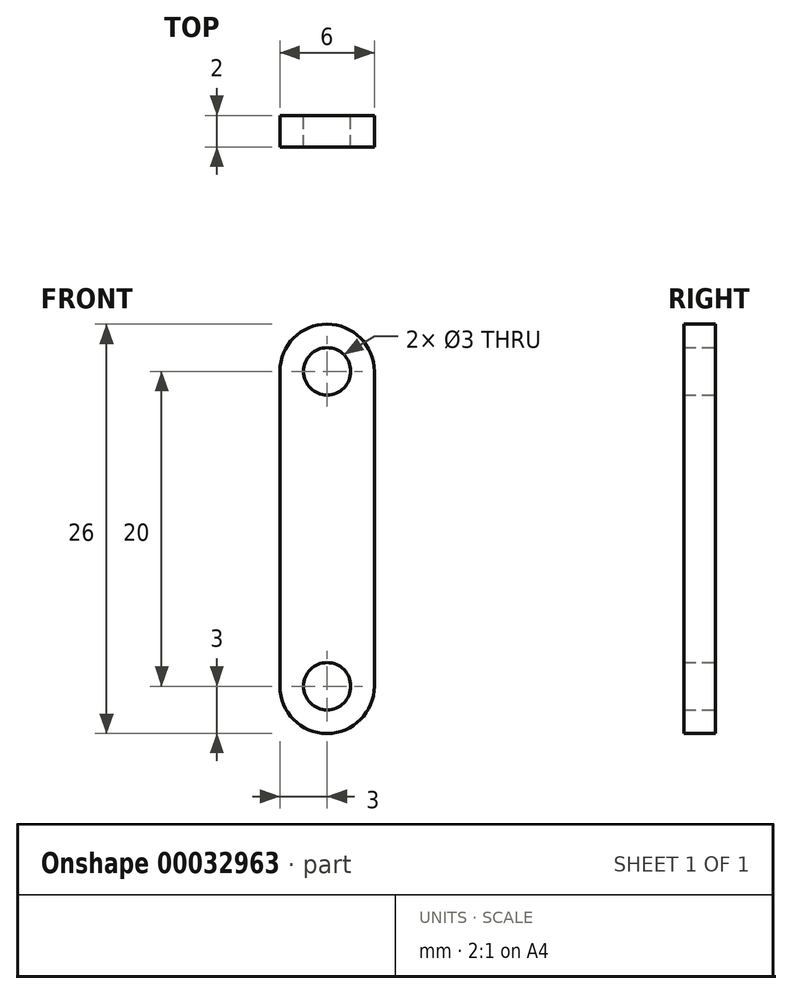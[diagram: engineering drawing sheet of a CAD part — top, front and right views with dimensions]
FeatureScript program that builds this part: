
annotation { "Feature Type Name" : "Feature", "Feature Type Description" : "" }
export const myFeature = defineFeature(function(context is Context, id is Id, definition is map)
    precondition{}
    {
        {
            var Q0;
            Q0=qCreatedBy(makeId("Front.planeOp"),FACE);
            var sketch = newSketch(context, id + "F0", { "sketchPlane" : qUnion([Q0])});
            skCircle(sketch, "E0", {"center": v(0, 10) * mm, "radius": 1.5 * mm});
            skArc(sketch, "E1.0", {"start": v(3, 10) * mm, "mid": v(0, 13) * mm, "end": v(-3, 10) * mm});
            skLineSegment(sketch, "E2", {"start": v(-3, 10) * mm, "end": v(3, 10) * mm, "construction": true});
            skLineSegment(sketch, "E3", {"start": v(-3, 10) * mm, "end": v(-3, 0) * mm});
            skLineSegment(sketch, "E4.MirrorCS", {"start": v(3, 10) * mm, "end": v(3, 0) * mm});
            skLineSegment(sketch, "E5.MirrorCS", {"start": v(3, -10) * mm, "end": v(3, 0) * mm});
            skLineSegment(sketch, "E6.MirrorCS", {"start": v(-3, -10) * mm, "end": v(-3, 0) * mm});
            skArc(sketch, "E7.MirrorCS", {"start": v(3, -10) * mm, "mid": v(0, -13) * mm, "end": v(-3, -10) * mm});
            skCircle(sketch, "E8.MirrorC", {"center": v(0, -10) * mm, "radius": 1.5 * mm});
            skSolve(sketch);
        }
        {
            var Q0;
            Q0=qSketchRegion(id+"F0",true);
            extrude(context, id + "F1", {"entities" : qUnion([Q0]), "depth" : 2 * mm});
        }
    });
